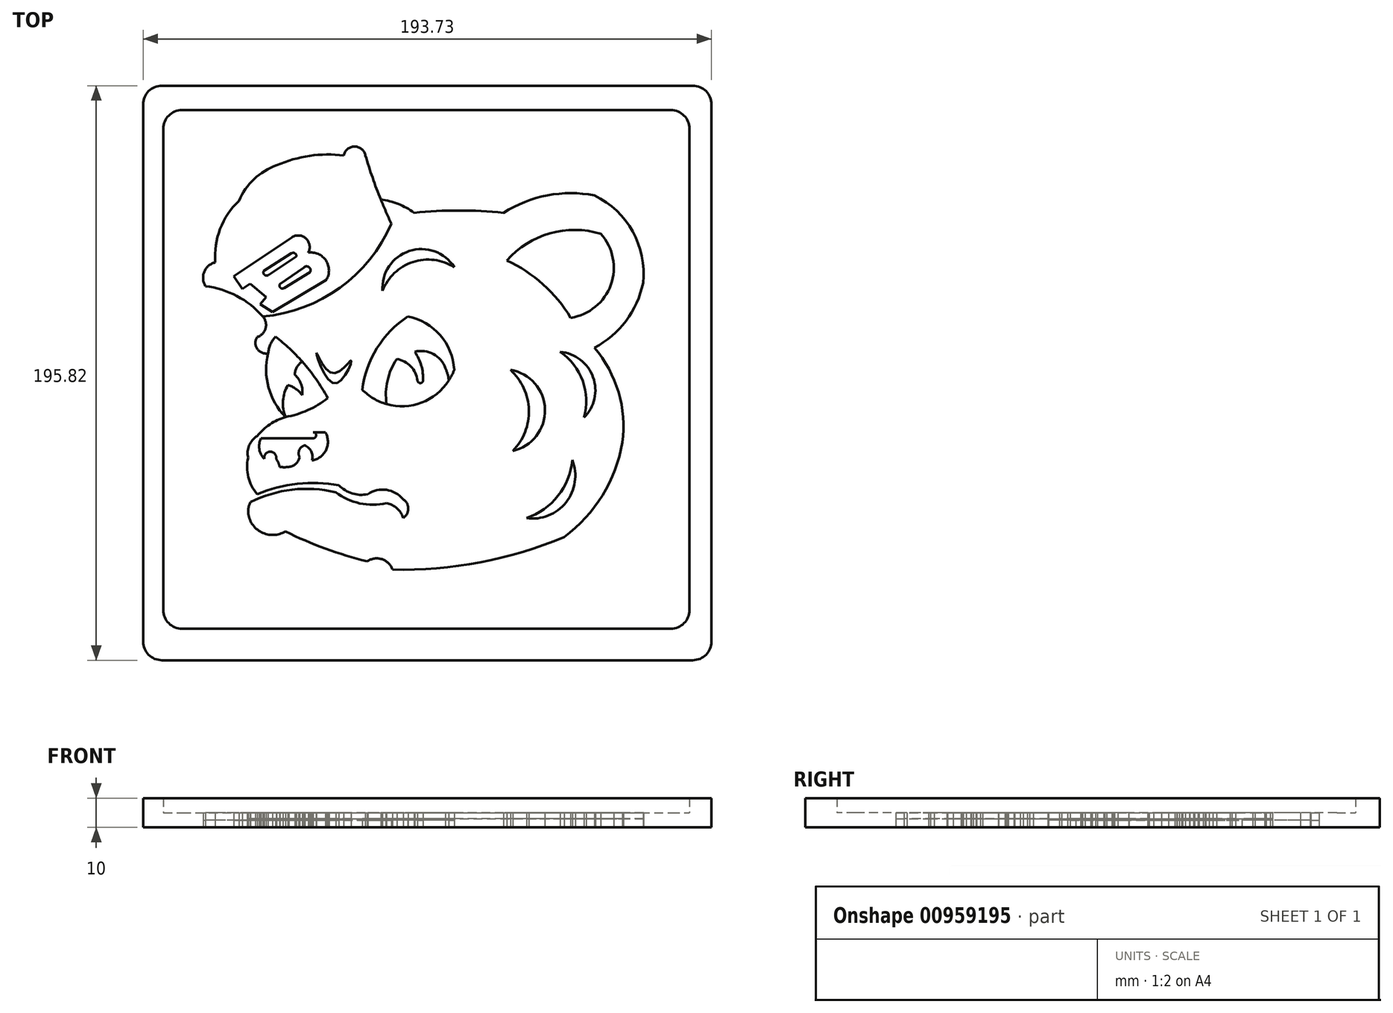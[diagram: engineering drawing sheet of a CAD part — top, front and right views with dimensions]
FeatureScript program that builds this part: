
annotation { "Feature Type Name" : "Feature", "Feature Type Description" : "" }
export const myFeature = defineFeature(function(context is Context, id is Id, definition is map)
    precondition{}
    {
        {
            var Q0;
            Q0=qCreatedBy(makeId("Top.planeOp"),FACE);
            var sketch = newSketch(context, id + "F0", { "sketchPlane" : qUnion([Q0])});
            skArc(sketch, "E0", {"start": v(-49.9, 69.78) * mm, "mid": v(-57.6, 65.05) * mm, "end": v(-62.79, 57.63) * mm});
            skArc(sketch, "E1", {"start": v(-62.79, 57.63) * mm, "mid": v(-54.31, 61.55) * mm, "end": v(-49.9, 69.78) * mm});
            skArc(sketch, "E2", {"start": v(-62.79, 57.63) * mm, "mid": v(-69.2, 48.05) * mm, "end": v(-70.87, 36.64) * mm});
            skArc(sketch, "E3", {"start": v(-27.04, 73.1) * mm, "mid": v(-38.7, 72.97) * mm, "end": v(-49.9, 69.78) * mm});
            skArc(sketch, "E4", {"start": v(-19.68, 73.1) * mm, "mid": v(-23.36, 76.16) * mm, "end": v(-27.04, 73.1) * mm});
            skArc(sketch, "E5", {"start": v(-70.87, 36.64) * mm, "mid": v(-74.62, 33.45) * mm, "end": v(-74.19, 28.54) * mm});
            skArc(sketch, "E6", {"start": v(-74.19, 28.54) * mm, "mid": v(-45.9, 49.55) * mm, "end": v(-19.68, 73.1) * mm});
            skArc(sketch, "E7", {"start": v(-54.67, 18.23) * mm, "mid": v(-63.47, 25.18) * mm, "end": v(-74.19, 28.54) * mm});
            skArc(sketch, "E8", {"start": v(-19.68, 73.1) * mm, "mid": v(-15.7, 61.33) * mm, "end": v(-10.84, 49.9) * mm});
            skArc(sketch, "E9", {"start": v(-54.67, 18.23) * mm, "mid": v(-28.37, 28) * mm, "end": v(-10.84, 49.9) * mm});
            skArc(sketch, "E10", {"start": v(-3.1, 53.58) * mm, "mid": v(-8.48, 56.56) * mm, "end": v(-14.43, 58.1) * mm});
            skArc(sketch, "E11", {"start": v(27.46, 53.58) * mm, "mid": v(12.18, 54.34) * mm, "end": v(-3.1, 53.58) * mm});
            skArc(sketch, "E12", {"start": v(58.4, 59.47) * mm, "mid": v(42.36, 59.5) * mm, "end": v(27.46, 53.58) * mm});
            skArc(sketch, "E13", {"start": v(74.97, 29.64) * mm, "mid": v(71.43, 47.2) * mm, "end": v(58.4, 59.47) * mm});
            skArc(sketch, "E14", {"start": v(58.4, 7.55) * mm, "mid": v(69.17, 16.73) * mm, "end": v(74.97, 29.64) * mm});
            skArc(sketch, "E15", {"start": v(67.93, -24.7) * mm, "mid": v(66.6, -7.56) * mm, "end": v(58.4, 7.55) * mm});
            skArc(sketch, "E16", {"start": v(48.11, -56.9) * mm, "mid": v(61.15, -42.73) * mm, "end": v(67.93, -24.7) * mm});
            skArc(sketch, "E17", {"start": v(-10.42, -68.06) * mm, "mid": v(19.43, -65.56) * mm, "end": v(48.11, -56.9) * mm});
            skArc(sketch, "E18", {"start": v(-10.42, -68.06) * mm, "mid": v(-14.07, -64.52) * mm, "end": v(-19.1, -65.27) * mm});
            skArc(sketch, "E19", {"start": v(-46.96, -55.05) * mm, "mid": v(-33.3, -60.91) * mm, "end": v(-19.1, -65.27) * mm});
            skArc(sketch, "E20", {"start": v(-59.66, -48.55) * mm, "mid": v(-55.12, -55.32) * mm, "end": v(-46.96, -55.05) * mm});
            skArc(sketch, "E21", {"start": v(-56.56, -42.35) * mm, "mid": v(-58.87, -45.07) * mm, "end": v(-59.66, -48.55) * mm});
            skArc(sketch, "E22", {"start": v(-59.66, -29.97) * mm, "mid": v(-59.57, -36.53) * mm, "end": v(-56.56, -42.35) * mm});
            skArc(sketch, "E23", {"start": v(-56.56, -22.54) * mm, "mid": v(-59.28, -25.76) * mm, "end": v(-59.66, -29.97) * mm});
            skArc(sketch, "E24", {"start": v(-46.96, -16.03) * mm, "mid": v(-52.26, -18.56) * mm, "end": v(-56.56, -22.54) * mm});
            skArc(sketch, "E25", {"start": v(-52.85, 5.64) * mm, "mid": v(-52.7, -5.95) * mm, "end": v(-46.96, -16.03) * mm});
            skArc(sketch, "E26", {"start": v(-56.56, 11.22) * mm, "mid": v(-56.56, 7.2) * mm, "end": v(-52.85, 5.64) * mm});
            skArc(sketch, "E27", {"start": v(-56.56, 11.22) * mm, "mid": v(-53.7, 14.2) * mm, "end": v(-54.67, 18.23) * mm});
            skArc(sketch, "E28", {"start": v(-5.26, 18.23) * mm, "mid": v(-15.73, 7.43) * mm, "end": v(-20.73, -6.76) * mm});
            skArc(sketch, "E29", {"start": v(10.58, 0) * mm, "mid": v(5.8, 11.85) * mm, "end": v(-5.26, 18.23) * mm});
            skArc(sketch, "E30", {"start": v(-20.73, -6.76) * mm, "mid": v(-3.23, -11.95) * mm, "end": v(10.58, 0) * mm});
            skArc(sketch, "E31", {"start": v(-8.96, 3.74) * mm, "mid": v(-12.15, -3.62) * mm, "end": v(-12.47, -11.64) * mm});
            skArc(sketch, "E32", {"start": v(-1.95, -3.63) * mm, "mid": v(-4.23, 1.23) * mm, "end": v(-8.96, 3.74) * mm});
            skArc(sketch, "E33", {"start": v(-1.95, -3.63) * mm, "mid": v(-0.97, -4.48) * mm, "end": v(0, -3.63) * mm});
            skArc(sketch, "E34", {"start": v(0, -3.63) * mm, "mid": v(-0.62, 1.5) * mm, "end": v(-2.87, 6.17) * mm});
            skArc(sketch, "E35", {"start": v(7.58, 0.6) * mm, "mid": v(3.46, 5.45) * mm, "end": v(-2.87, 6.17) * mm});
            skArc(sketch, "E36", {"start": v(8.76, -3.63) * mm, "mid": v(8.34, -1.47) * mm, "end": v(7.58, 0.6) * mm});
            skArc(sketch, "E37", {"start": v(-46.08, -5.13) * mm, "mid": v(-47.76, -10.48) * mm, "end": v(-46.96, -16.03) * mm});
            skArc(sketch, "E38", {"start": v(-41.2, -8.64) * mm, "mid": v(-43.36, -6.5) * mm, "end": v(-46.08, -5.13) * mm});
            skArc(sketch, "E39", {"start": v(-41.2, -8.64) * mm, "mid": v(-41.6, -4.84) * mm, "end": v(-43.73, -1.68) * mm});
            skArc(sketch, "E40", {"start": v(-46.96, -16.03) * mm, "mid": v(-39.33, -13.72) * mm, "end": v(-32.53, -9.55) * mm});
            skArc(sketch, "E41", {"start": v(-32.53, -9.55) * mm, "mid": v(-40.33, 1.82) * mm, "end": v(-50.31, 11.33) * mm});
            skArc(sketch, "E42", {"start": v(-50.31, 11.33) * mm, "mid": v(-52.05, 8.7) * mm, "end": v(-52.85, 5.64) * mm});
            skArc(sketch, "E43", {"start": v(-41.2, 2.82) * mm, "mid": v(-43.05, 0.9) * mm, "end": v(-43.73, -1.68) * mm});
            skLineSegment(sketch, "E44", {"start": v(-55.24, -23.3) * mm, "end": v(-37.5, -23.3) * mm});
            skArc(sketch, "E45", {"start": v(-37.5, -23.3) * mm, "mid": v(-36.46, -22.26) * mm, "end": v(-37.5, -21.22) * mm});
            skLineSegment(sketch, "E46", {"start": v(-37.5, -21.22) * mm, "end": v(-33.34, -21.22) * mm});
            skArc(sketch, "E47", {"start": v(-37.83, -30.85) * mm, "mid": v(-33.07, -27.21) * mm, "end": v(-33.34, -21.22) * mm});
            skArc(sketch, "E48", {"start": v(-37.83, -30.85) * mm, "mid": v(-38.13, -27.81) * mm, "end": v(-40.35, -25.7) * mm});
            skArc(sketch, "E49", {"start": v(-40.35, -25.7) * mm, "mid": v(-42.2, -27.3) * mm, "end": v(-42.07, -29.74) * mm});
            skArc(sketch, "E50", {"start": v(-45.73, -33.06) * mm, "mid": v(-43.38, -31.97) * mm, "end": v(-42.07, -29.74) * mm});
            skArc(sketch, "E51", {"start": v(-48.9, -33.06) * mm, "mid": v(-47.3, -33.16) * mm, "end": v(-45.73, -33.06) * mm});
            skArc(sketch, "E52", {"start": v(-55.24, -23.3) * mm, "mid": v(-55.83, -26.98) * mm, "end": v(-54.15, -30.3) * mm});
            skArc(sketch, "E53", {"start": v(-50.1, -30.3) * mm, "mid": v(-52.12, -27.88) * mm, "end": v(-54.15, -30.3) * mm});
            skArc(sketch, "E54", {"start": v(-48.9, -33.06) * mm, "mid": v(-49.37, -31.63) * mm, "end": v(-50.1, -30.3) * mm});
            skArc(sketch, "E55", {"start": v(-28.72, -39.28) * mm, "mid": v(-42.87, -38.8) * mm, "end": v(-56.56, -42.35) * mm});
            skArc(sketch, "E56", {"start": v(-28.72, -39.28) * mm, "mid": v(-24.2, -42.1) * mm, "end": v(-18.87, -42.35) * mm});
            skArc(sketch, "E57", {"start": v(-6.82, -44.1) * mm, "mid": v(-12.5, -40.88) * mm, "end": v(-18.87, -42.35) * mm});
            skArc(sketch, "E58", {"start": v(-6.82, -50.45) * mm, "mid": v(-5.07, -47.27) * mm, "end": v(-6.82, -44.1) * mm});
            skArc(sketch, "E59", {"start": v(-6.82, -50.45) * mm, "mid": v(-8.97, -47.14) * mm, "end": v(-12.52, -45.41) * mm});
            skArc(sketch, "E60", {"start": v(-29.82, -41.69) * mm, "mid": v(-21.58, -45.47) * mm, "end": v(-12.52, -45.41) * mm});
            skArc(sketch, "E61", {"start": v(-29.82, -41.69) * mm, "mid": v(-44.64, -40.8) * mm, "end": v(-58.87, -45.07) * mm});
            skArc(sketch, "E62", {"start": v(35.22, -50.52) * mm, "mid": v(45.94, -42.92) * mm, "end": v(50.85, -30.73) * mm});
            skArc(sketch, "E63", {"start": v(35.22, -50.52) * mm, "mid": v(48.72, -45.12) * mm, "end": v(50.85, -30.73) * mm});
            skArc(sketch, "E64", {"start": v(30.53, -27.6) * mm, "mid": v(36.06, -13.63) * mm, "end": v(29.75, 0) * mm});
            skArc(sketch, "E65", {"start": v(30.53, -27.6) * mm, "mid": v(41.54, -13.48) * mm, "end": v(29.75, 0) * mm});
            skArc(sketch, "E66", {"start": v(54.85, -16.26) * mm, "mid": v(57.93, -2.47) * mm, "end": v(46.75, 6.17) * mm});
            skArc(sketch, "E67", {"start": v(54.85, -16.26) * mm, "mid": v(54.4, -3.74) * mm, "end": v(46.75, 6.17) * mm});
            skArc(sketch, "E68", {"start": v(50.3, 17.78) * mm, "mid": v(40.88, 29.17) * mm, "end": v(28.53, 37.3) * mm});
            skArc(sketch, "E69", {"start": v(50.3, 17.78) * mm, "mid": v(63.97, 29.04) * mm, "end": v(60.56, 46.4) * mm});
            skArc(sketch, "E70", {"start": v(60.56, 46.4) * mm, "mid": v(43.2, 46.56) * mm, "end": v(28.53, 37.3) * mm});
            skArc(sketch, "E71", {"start": v(10.63, 35) * mm, "mid": v(-3.5, 36.77) * mm, "end": v(-13.84, 26.96) * mm});
            skArc(sketch, "E72", {"start": v(10.63, 35) * mm, "mid": v(-4.74, 40.53) * mm, "end": v(-13.84, 26.96) * mm});
            skFitSpline(sketch, "E73", {"points": [v(-36.4, 5.8) * mm, v(-30.22, -4.6) * mm, v(-24.53, 3.17) * mm, v(-30.77, -1.15) * mm, v(-36.4, 5.8) * mm]});
            skLineSegment(sketch, "E74", {"start": v(-64.52, 31.99) * mm, "end": v(-44.76, 45.18) * mm});
            skLineSegment(sketch, "E75", {"start": v(-64.52, 31.99) * mm, "end": v(-61.6, 27.61) * mm});
            skLineSegment(sketch, "E76", {"start": v(-61.6, 27.61) * mm, "end": v(-58.91, 29.4) * mm});
            skLineSegment(sketch, "E77", {"start": v(-58.91, 29.4) * mm, "end": v(-53.45, 24.82) * mm});
            skLineSegment(sketch, "E78", {"start": v(-53.45, 24.82) * mm, "end": v(-55.48, 22.4) * mm});
            skLineSegment(sketch, "E79", {"start": v(-55.48, 22.4) * mm, "end": v(-51.35, 19.74) * mm});
            skLineSegment(sketch, "E80", {"start": v(-51.35, 19.74) * mm, "end": v(-33.05, 30.6) * mm});
            skArc(sketch, "E81", {"start": v(-39.22, 39.96) * mm, "mid": v(-39.9, 44.78) * mm, "end": v(-44.76, 45.18) * mm});
            skArc(sketch, "E82", {"start": v(-33.05, 30.6) * mm, "mid": v(-33.11, 37.28) * mm, "end": v(-39.22, 39.96) * mm});
            skLineSegment(sketch, "E83", {"start": v(-54.33, 33.77) * mm, "end": v(-44.83, 39.76) * mm});
            skArc(sketch, "E84", {"start": v(-43.27, 38.64) * mm, "mid": v(-43.67, 39.72) * mm, "end": v(-44.83, 39.76) * mm});
            skLineSegment(sketch, "E85", {"start": v(-43.27, 38.64) * mm, "end": v(-52.77, 32.34) * mm});
            skArc(sketch, "E86", {"start": v(-54.33, 33.77) * mm, "mid": v(-54.11, 32.44) * mm, "end": v(-52.77, 32.34) * mm});
            skLineSegment(sketch, "E87", {"start": v(-48.82, 29.29) * mm, "end": v(-40.7, 34.9) * mm});
            skArc(sketch, "E88", {"start": v(-38.52, 33.37) * mm, "mid": v(-38.95, 35.07) * mm, "end": v(-40.7, 34.9) * mm});
            skLineSegment(sketch, "E89", {"start": v(-38.52, 33.37) * mm, "end": v(-47.4, 27.9) * mm});
            skArc(sketch, "E90", {"start": v(-48.82, 29.29) * mm, "mid": v(-48.66, 28.04) * mm, "end": v(-47.4, 27.9) * mm});
            skLineSegment(sketch, "E91.bottom", {"start": v(-82.22, 88.57) * mm, "end": v(84.42, 88.57) * mm});
            skLineSegment(sketch, "E91.top", {"start": v(-82.22, -88.2) * mm, "end": v(84.42, -88.2) * mm});
            skLineSegment(sketch, "E91.left", {"start": v(-88.57, 82.22) * mm, "end": v(-88.57, -81.85) * mm});
            skLineSegment(sketch, "E91.right", {"start": v(90.77, 82.22) * mm, "end": v(90.77, -81.85) * mm});
            skLineSegment(sketch, "E92.bottom", {"start": v(-89.1, 96.88) * mm, "end": v(91.94, 96.88) * mm});
            skLineSegment(sketch, "E92.top", {"start": v(-89.1, -98.94) * mm, "end": v(91.94, -98.94) * mm});
            skLineSegment(sketch, "E92.left", {"start": v(-95.44, 90.53) * mm, "end": v(-95.44, -92.59) * mm});
            skLineSegment(sketch, "E92.right", {"start": v(98.3, 90.53) * mm, "end": v(98.3, -92.59) * mm});
            skPoint(sketch, "E93.visualSharp", {"position": v(-88.57, 88.57) * mm});
            skArc(sketch, "E93.filletArc", {"start": v(-82.22, 88.57) * mm, "mid": v(-86.7, 86.7) * mm, "end": v(-88.57, 82.22) * mm});
            skPoint(sketch, "E94.visualSharp", {"position": v(-95.44, 96.88) * mm});
            skArc(sketch, "E94.filletArc", {"start": v(-89.1, 96.88) * mm, "mid": v(-93.58, 95.02) * mm, "end": v(-95.44, 90.53) * mm});
            skPoint(sketch, "E95.visualSharp", {"position": v(-95.44, -98.94) * mm});
            skArc(sketch, "E95.filletArc", {"start": v(-95.44, -92.59) * mm, "mid": v(-93.58, -97.08) * mm, "end": v(-89.1, -98.94) * mm});
            skPoint(sketch, "E96.visualSharp", {"position": v(-88.57, -88.2) * mm});
            skArc(sketch, "E96.filletArc", {"start": v(-88.57, -81.85) * mm, "mid": v(-86.7, -86.34) * mm, "end": v(-82.22, -88.2) * mm});
            skPoint(sketch, "E97.visualSharp", {"position": v(98.3, -98.94) * mm});
            skArc(sketch, "E97.filletArc", {"start": v(91.94, -98.94) * mm, "mid": v(96.43, -97.08) * mm, "end": v(98.3, -92.59) * mm});
            skPoint(sketch, "E98.visualSharp", {"position": v(90.77, -88.2) * mm});
            skArc(sketch, "E98.filletArc", {"start": v(84.42, -88.2) * mm, "mid": v(88.92, -86.34) * mm, "end": v(90.77, -81.85) * mm});
            skPoint(sketch, "E99.visualSharp", {"position": v(90.77, 88.57) * mm});
            skArc(sketch, "E99.filletArc", {"start": v(90.77, 82.22) * mm, "mid": v(88.92, 86.7) * mm, "end": v(84.42, 88.57) * mm});
            skPoint(sketch, "E100.visualSharp", {"position": v(98.3, 96.88) * mm});
            skArc(sketch, "E100.filletArc", {"start": v(98.3, 90.53) * mm, "mid": v(96.43, 95.02) * mm, "end": v(91.94, 96.88) * mm});
            skSolve(sketch);
        }
        {
            var Q0;
            Q0=makeQuery(id+"F0.imprint","IMPRINT",FACE,{"disambiguationData":[TD([[makeQuery(id+"F0.imprint","IMPRINT",EDGE,{"derivedFrom":sQuery(id+"F0.wireOp",EDGE,"E0")}),-1.0]])]});
            var Q1;
            {var subQ0=sQuery(id+"F0.wireOp",EDGE,"E55");Q1=makeQuery(id+"F0.imprint","IMPRINT",FACE,{"disambiguationData":[TD([[makeQuery(id+"F0.imprint","IMPRINT",EDGE,{"derivedFrom":subQ0}),1.0]])]});}
            var Q2;
            Q2=makeQuery(id+"F0.imprint","IMPRINT",FACE,{"disambiguationData":[TD([[makeQuery(id+"F0.imprint","IMPRINT",EDGE,{"derivedFrom":sQuery(id+"F0.wireOp",EDGE,"E62")}),-1.0]])]});
            var Q3;
            Q3=makeQuery(id+"F0.imprint","IMPRINT",FACE,{"disambiguationData":[TD([[makeQuery(id+"F0.imprint","IMPRINT",EDGE,{"derivedFrom":sQuery(id+"F0.wireOp",EDGE,"E64")}),-1.0]])]});
            var Q4;
            Q4=makeQuery(id+"F0.imprint","IMPRINT",FACE,{"disambiguationData":[TD([[makeQuery(id+"F0.imprint","IMPRINT",EDGE,{"derivedFrom":sQuery(id+"F0.wireOp",EDGE,"E44")}),-1.0]])]});
            var Q5;
            Q5=makeQuery(id+"F0.imprint","IMPRINT",FACE,{"disambiguationData":[TD([[makeQuery(id+"F0.imprint","IMPRINT",EDGE,{"derivedFrom":sQuery(id+"F0.wireOp",EDGE,"E68")}),-1.0]])]});
            var Q6;
            Q6=makeQuery(id+"F0.imprint","IMPRINT",FACE,{"disambiguationData":[TD([[makeQuery(id+"F0.imprint","IMPRINT",EDGE,{"derivedFrom":sQuery(id+"F0.wireOp",EDGE,"E66")}),1.0]])]});
            var Q7;
            Q7=makeQuery(id+"F0.imprint","IMPRINT",FACE,{"disambiguationData":[TD([[makeQuery(id+"F0.imprint","IMPRINT",EDGE,{"derivedFrom":sQuery(id+"F0.wireOp",EDGE,"E71")}),-1.0]])]});
            var Q8;
            Q8=makeQuery(id+"F0.imprint","IMPRINT",FACE,{"disambiguationData":[TD([[makeQuery(id+"F0.imprint","IMPRINT",EDGE,{"derivedFrom":sQuery(id+"F0.wireOp",EDGE,"E74")}),-1.0]])]});
            var Q9;
            Q9=makeQuery(id+"F0.imprint","IMPRINT",FACE,{"disambiguationData":[TD([[makeQuery(id+"F0.imprint","IMPRINT",EDGE,{"derivedFrom":sQuery(id+"F0.wireOp",EDGE,"E37")}),1.0]])]});
            var Q10;
            {var subQ0=sQuery(id+"F0.wireOp",EDGE,"E31");Q10=makeQuery(id+"F0.imprint","IMPRINT",FACE,{"disambiguationData":[TD([[makeQuery(id+"F0.imprint","IMPRINT",EDGE,{"derivedFrom":subQ0}),1.0]])]});}
            var Q11;
            Q11=makeQuery(id+"F0.imprint","IMPRINT",FACE,{"disambiguationData":[TD([[makeQuery(id+"F0.imprint","IMPRINT",EDGE,{"derivedFrom":sQuery(id+"F0.wireOp",EDGE,"E73")}),1.0]])]});
            extrude(context, id + "F1", {"entities" : qUnion([Q0, Q1, Q2, Q3, Q4, Q5, Q6, Q7, Q8, Q9, Q10, Q11]), "depth" : 5 * mm, "offsetDistance" : 25.4 * mm});
        }
        {
            var Q0;
            {var subQ8=sQuery(id+"F0.wireOp",EDGE,"E9");Q0=makeQuery(id+"F0.imprint","IMPRINT",FACE,{"disambiguationData":[TD([[makeQuery(id+"F0.imprint","IMPRINT",EDGE,{"derivedFrom":subQ8}),-1.0]])]});}
            extrude(context, id + "F2", {"entities" : qUnion([Q0]), "depth" : 3 * mm, "offsetDistance" : 25.4 * mm});
        }
        {
            var Q0;
            {var subQ3=sQuery(id+"F0.wireOp",EDGE,"E28");Q0=makeQuery(id+"F0.imprint","IMPRINT",FACE,{"disambiguationData":[TD([[makeQuery(id+"F0.imprint","IMPRINT",EDGE,{"derivedFrom":subQ3}),1.0]])]});}
            var Q1;
            Q1=makeQuery(id+"F0.imprint","IMPRINT",FACE,{"disambiguationData":[TD([[makeQuery(id+"F0.imprint","IMPRINT",EDGE,{"derivedFrom":sQuery(id+"F0.wireOp",EDGE,"E25")}),1.0]])]});
            var Q2;
            Q2=makeQuery(id+"F0.imprint","IMPRINT",FACE,{"disambiguationData":[TD([[makeQuery(id+"F0.imprint","IMPRINT",EDGE,{"derivedFrom":sQuery(id+"F0.wireOp",EDGE,"E0")}),1.0]])]});
            var Q3;
            Q3=makeQuery(id+"F0.imprint","IMPRINT",FACE,{"disambiguationData":[TD([[makeQuery(id+"F0.imprint","IMPRINT",EDGE,{"derivedFrom":sQuery(id+"F0.wireOp",EDGE,"E1")}),-1.0]])]});
            var Q4;
            {var subQ1=sQuery(id+"F0.wireOp",EDGE,"E6");Q4=makeQuery(id+"F0.imprint","IMPRINT",FACE,{"disambiguationData":[TD([[makeQuery(id+"F0.imprint","IMPRINT",EDGE,{"derivedFrom":subQ1}),-1.0]])]});}
            var Q5;
            Q5=makeQuery(id+"F0.imprint","IMPRINT",FACE,{"disambiguationData":[TD([[makeQuery(id+"F0.imprint","IMPRINT",EDGE,{"derivedFrom":sQuery(id+"F0.wireOp",EDGE,"E87")}),-1.0]])]});
            var Q6;
            Q6=makeQuery(id+"F0.imprint","IMPRINT",FACE,{"disambiguationData":[TD([[makeQuery(id+"F0.imprint","IMPRINT",EDGE,{"derivedFrom":sQuery(id+"F0.wireOp",EDGE,"E83")}),-1.0]])]});
            extrude(context, id + "F3", {"entities" : qUnion([Q0, Q1, Q2, Q3, Q4, Q5, Q6]), "depth" : 2.5 * mm, "offsetDistance" : 25.4 * mm});
        }
        {
            var Q0;
            Q0=makeQuery(id+"F0.imprint","IMPRINT",FACE,{"disambiguationData":[TD([[makeQuery(id+"F0.imprint","IMPRINT",EDGE,{"derivedFrom":sQuery(id+"F0.wireOp",EDGE,"E91.bottom")}),1.0]])]});
            extrude(context, id + "F4", {"entities" : qUnion([Q0]), "operationType" : NewBodyOperationType.ADD, "depth" : 10 * mm, "offsetDistance" : 25.4 * mm});
        }
    });
